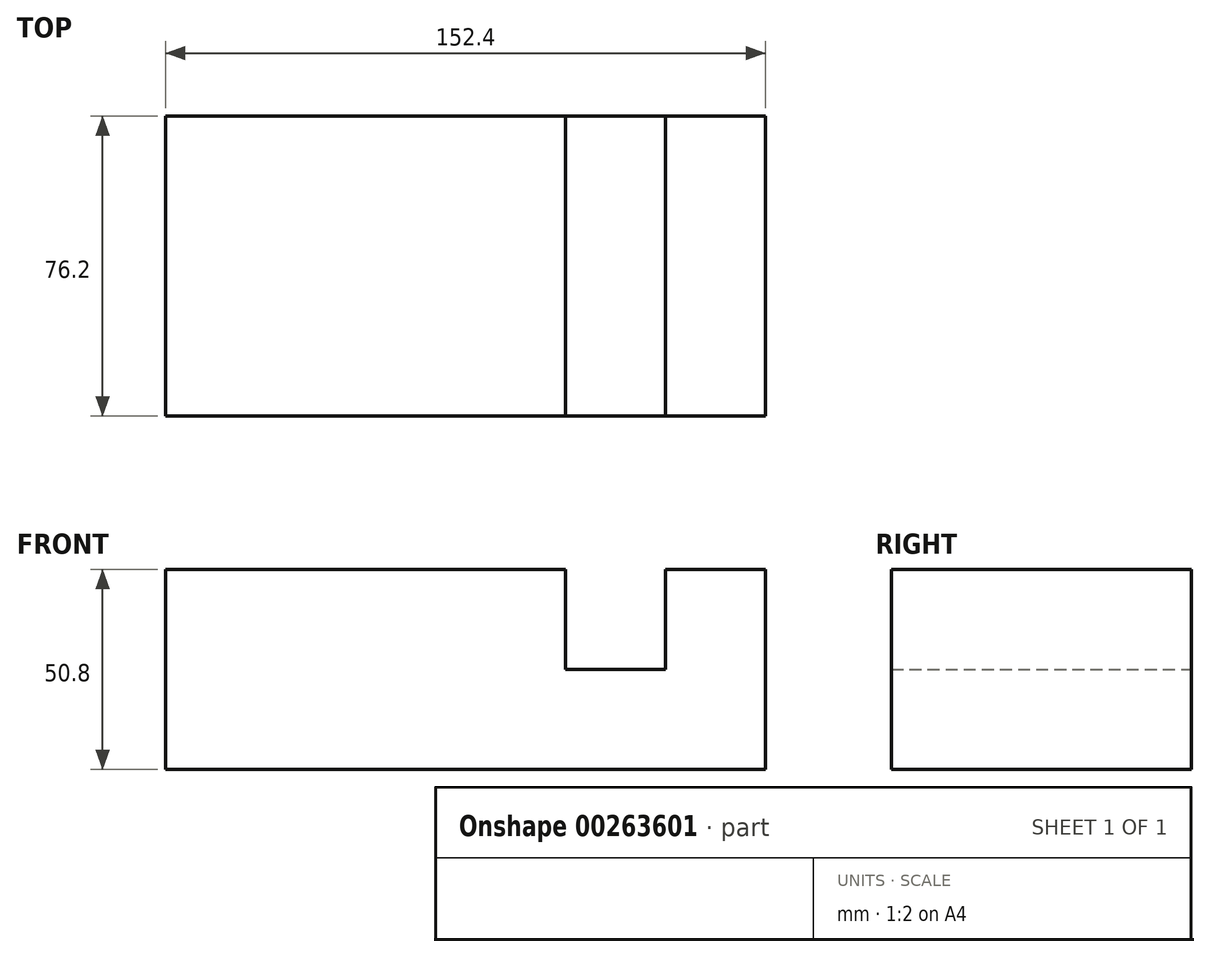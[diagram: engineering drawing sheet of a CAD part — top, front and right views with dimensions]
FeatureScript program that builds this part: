
annotation { "Feature Type Name" : "Feature", "Feature Type Description" : "" }
export const myFeature = defineFeature(function(context is Context, id is Id, definition is map)
    precondition{}
    {
        {
            var Q0;
            Q0=qCreatedBy(makeId("Front.planeOp"),FACE);
            var sketch = newSketch(context, id + "F0", { "sketchPlane" : qUnion([Q0])});
            skLineSegment(sketch, "E0.bottom", {"start": v(-75.98, 0) * mm, "end": v(76.42, 0) * mm});
            skLineSegment(sketch, "E0.left", {"start": v(-75.98, 0) * mm, "end": v(-75.98, 50.8) * mm});
            skLineSegment(sketch, "E1", {"start": v(-75.98, 50.8) * mm, "end": v(25.62, 50.8) * mm});
            skLineSegment(sketch, "E2", {"start": v(25.62, 50.8) * mm, "end": v(25.62, 25.4) * mm});
            skLineSegment(sketch, "E3", {"start": v(25.62, 25.4) * mm, "end": v(51.02, 25.4) * mm});
            skLineSegment(sketch, "E4", {"start": v(51.02, 25.4) * mm, "end": v(51.02, 50.8) * mm});
            skLineSegment(sketch, "E5", {"start": v(51.02, 50.8) * mm, "end": v(76.42, 50.8) * mm});
            skLineSegment(sketch, "E6", {"start": v(76.42, 50.8) * mm, "end": v(76.42, 0) * mm});
            skSolve(sketch);
        }
        {
            var Q0;
            Q0 = qSketchRegion(id + "F0", true);
            extrude(context, id + "F1", {"entities" : qUnion([Q0]), "depth" : 76.2 * mm});
        }
    });
